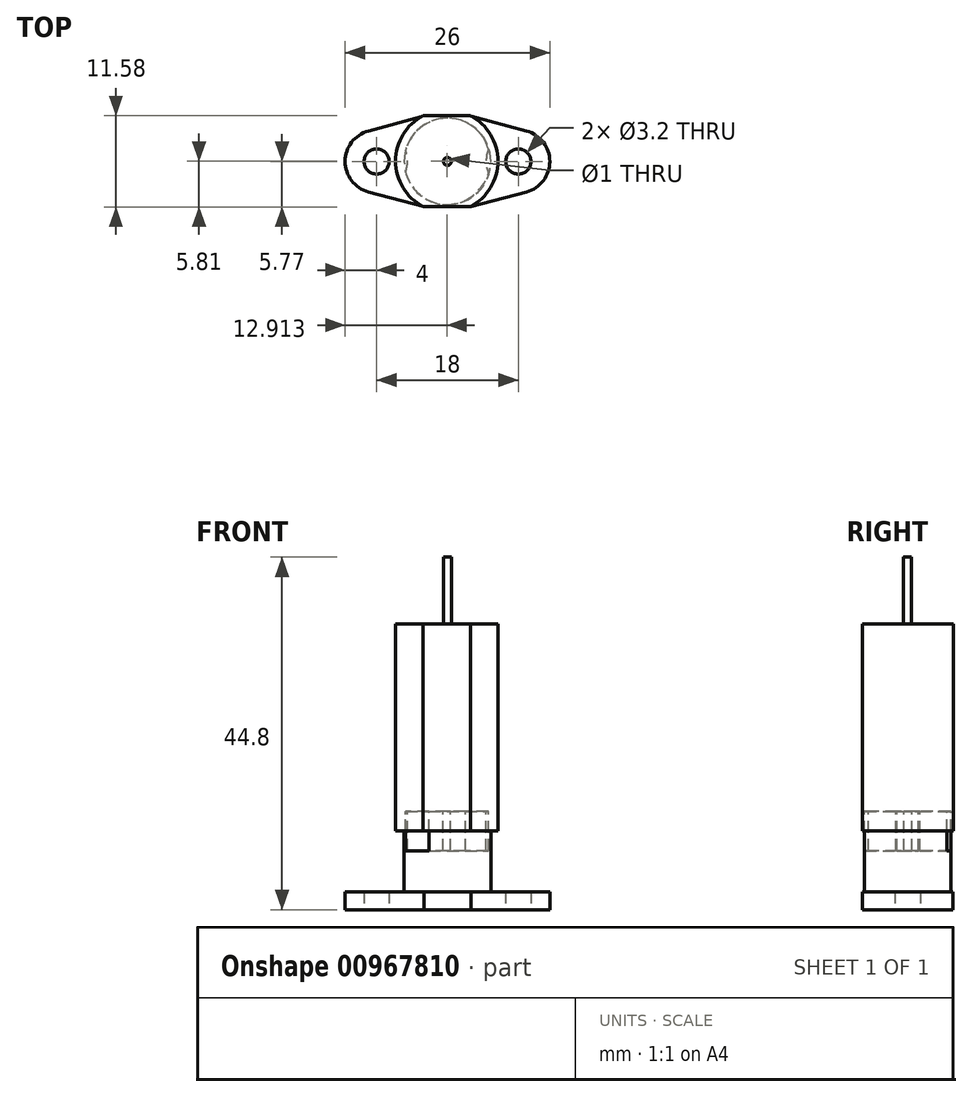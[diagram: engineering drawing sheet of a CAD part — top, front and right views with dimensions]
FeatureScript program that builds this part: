
annotation { "Feature Type Name" : "Feature", "Feature Type Description" : "" }
export const myFeature = defineFeature(function(context is Context, id is Id, definition is map)
    precondition{}
    {
        {
            var Q0;
            Q0=qCreatedBy(makeId("Top.planeOp"),FACE);
            var sketch = newSketch(context, id + "F0", { "sketchPlane" : qUnion([Q0])});
            skCircle(sketch, "E0", {"center": v(9, 0) * mm, "radius": 1.6 * mm});
            skCircle(sketch, "E1", {"center": v(-9, 0) * mm, "radius": 1.6 * mm});
            skCircle(sketch, "E2", {"center": v(9, 0) * mm, "radius": 4 * mm});
            skCircle(sketch, "E3", {"center": v(-9, 0) * mm, "radius": 4 * mm});
            skLineSegment(sketch, "E4.bottom", {"start": v(3, 5.77) * mm, "end": v(-3, 5.77) * mm});
            skLineSegment(sketch, "E4.top", {"start": v(3, -5.76) * mm, "end": v(-3, -5.76) * mm});
            skPoint(sketch, "E4.middle", {"position": v(0, 0) * mm});
            skLineSegment(sketch, "E5", {"start": v(3, 5.77) * mm, "end": v(10.04, 3.86) * mm});
            skLineSegment(sketch, "E6", {"start": v(3, -5.76) * mm, "end": v(10.04, -3.86) * mm});
            skLineSegment(sketch, "E7", {"start": v(-3, -5.76) * mm, "end": v(-10.04, -3.86) * mm});
            skLineSegment(sketch, "E8", {"start": v(-3, 5.77) * mm, "end": v(-10.04, 3.86) * mm});
            skCircle(sketch, "E9", {"center": v(0, 0) * mm, "radius": 6.5 * mm});
            skCircle(sketch, "E10", {"center": v(0, 0) * mm, "radius": 0.5 * mm});
            skCircle(sketch, "E11", {"center": v(0, 0) * mm, "radius": 5.5 * mm});
            skSolve(sketch);
        }
        {
            var Q0;
            Q0=makeQuery(id+"F0.imprint","IMPRINT",FACE,{"disambiguationData":[TD([[makeQuery(id+"F0.imprint","IMPRINT",EDGE,{"derivedFrom":sQuery(id+"F0.wireOp",EDGE,"E1")}),-1.0]])]});
            var Q1;
            {var subQ0=sQuery(id+"F0.wireOp",EDGE,"E8");var subQ1=sQuery(id+"F0.wireOp",EDGE,"E3");var subQ2=makeQuery(id+"F0.imprint","INTERSECT",VERTEX,{"derivedFrom":[subQ1,subQ0]});Q1=makeQuery(id+"F0.imprint","IMPRINT",FACE,{"disambiguationData":[TD([[makeQuery(id+"F0.imprint","IMPRINT",EDGE,{"disambiguationData":[TD([[subQ2,1.0]])],"derivedFrom":subQ1}),-1.0]])]});}
            var Q2;
            {var subQ0=sQuery(id+"F0.wireOp",EDGE,"E9");var subQ1=sQuery(id+"F0.wireOp",EDGE,"E3");var subQ2=makeQuery(id+"F0.imprint","INTERSECT",VERTEX,{"disambiguationData":[OD(0.0)],"derivedFrom":[subQ1,subQ0]});Q2=makeQuery(id+"F0.imprint","IMPRINT",FACE,{"disambiguationData":[TD([[makeQuery(id+"F0.imprint","IMPRINT",EDGE,{"disambiguationData":[TD([[subQ2,1.0]])],"derivedFrom":subQ1}),1.0]])]});}
            var Q3;
            {var subQ0=sQuery(id+"F0.wireOp",EDGE,"E11");var subQ1=sQuery(id+"F0.wireOp",EDGE,"E3");var subQ2=makeQuery(id+"F0.imprint","INTERSECT",VERTEX,{"disambiguationData":[OD(0.0)],"derivedFrom":[subQ1,subQ0]});Q3=makeQuery(id+"F0.imprint","IMPRINT",FACE,{"disambiguationData":[TD([[makeQuery(id+"F0.imprint","IMPRINT",EDGE,{"disambiguationData":[TD([[subQ2,1.0]])],"derivedFrom":subQ1}),1.0]])]});}
            var Q4;
            {var subQ0=sQuery(id+"F0.wireOp",EDGE,"E7");var subQ1=sQuery(id+"F0.wireOp",EDGE,"E3");var subQ2=makeQuery(id+"F0.imprint","INTERSECT",VERTEX,{"derivedFrom":[subQ1,subQ0]});Q4=makeQuery(id+"F0.imprint","IMPRINT",FACE,{"disambiguationData":[TD([[makeQuery(id+"F0.imprint","IMPRINT",EDGE,{"disambiguationData":[TD([[subQ2,-1.0]])],"derivedFrom":subQ1}),-1.0]])]});}
            var Q5;
            {var subQ1=sQuery(id+"F0.wireOp",EDGE,"E4.top");Q5=makeQuery(id+"F0.imprint","IMPRINT",FACE,{"disambiguationData":[TD([[makeQuery(id+"F0.imprint","IMPRINT",EDGE,{"derivedFrom":subQ1}),-1.0]])]});}
            var Q6;
            Q6=makeQuery(id+"F0.imprint","IMPRINT",FACE,{"disambiguationData":[TD([[makeQuery(id+"F0.imprint","IMPRINT",EDGE,{"derivedFrom":sQuery(id+"F0.wireOp",EDGE,"E10")}),-1.0]])]});
            var Q7;
            {var subQ1=sQuery(id+"F0.wireOp",EDGE,"E4.bottom");Q7=makeQuery(id+"F0.imprint","IMPRINT",FACE,{"disambiguationData":[TD([[makeQuery(id+"F0.imprint","IMPRINT",EDGE,{"derivedFrom":subQ1}),1.0]])]});}
            var Q8;
            {var subQ0=sQuery(id+"F0.wireOp",EDGE,"E5");var subQ1=sQuery(id+"F0.wireOp",EDGE,"E2");var subQ2=makeQuery(id+"F0.imprint","INTERSECT",VERTEX,{"derivedFrom":[subQ1,subQ0]});Q8=makeQuery(id+"F0.imprint","IMPRINT",FACE,{"disambiguationData":[TD([[makeQuery(id+"F0.imprint","IMPRINT",EDGE,{"disambiguationData":[TD([[subQ2,-1.0]])],"derivedFrom":subQ1}),-1.0]])]});}
            var Q9;
            {var subQ0=sQuery(id+"F0.wireOp",EDGE,"E11");var subQ1=sQuery(id+"F0.wireOp",EDGE,"E2");var subQ2=makeQuery(id+"F0.imprint","INTERSECT",VERTEX,{"disambiguationData":[OD(0.0)],"derivedFrom":[subQ1,subQ0]});Q9=makeQuery(id+"F0.imprint","IMPRINT",FACE,{"disambiguationData":[TD([[makeQuery(id+"F0.imprint","IMPRINT",EDGE,{"disambiguationData":[TD([[subQ2,-1.0]])],"derivedFrom":subQ1}),1.0]])]});}
            var Q10;
            {var subQ0=sQuery(id+"F0.wireOp",EDGE,"E9");var subQ1=sQuery(id+"F0.wireOp",EDGE,"E2");var subQ2=makeQuery(id+"F0.imprint","INTERSECT",VERTEX,{"disambiguationData":[OD(0.0)],"derivedFrom":[subQ1,subQ0]});Q10=makeQuery(id+"F0.imprint","IMPRINT",FACE,{"disambiguationData":[TD([[makeQuery(id+"F0.imprint","IMPRINT",EDGE,{"disambiguationData":[TD([[subQ2,-1.0]])],"derivedFrom":subQ1}),1.0]])]});}
            var Q11;
            Q11=makeQuery(id+"F0.imprint","IMPRINT",FACE,{"disambiguationData":[TD([[makeQuery(id+"F0.imprint","IMPRINT",EDGE,{"derivedFrom":sQuery(id+"F0.wireOp",EDGE,"E0")}),-1.0]])]});
            var Q12;
            {var subQ0=sQuery(id+"F0.wireOp",EDGE,"E6");var subQ1=sQuery(id+"F0.wireOp",EDGE,"E2");var subQ2=makeQuery(id+"F0.imprint","INTERSECT",VERTEX,{"derivedFrom":[subQ1,subQ0]});Q12=makeQuery(id+"F0.imprint","IMPRINT",FACE,{"disambiguationData":[TD([[makeQuery(id+"F0.imprint","IMPRINT",EDGE,{"disambiguationData":[TD([[subQ2,1.0]])],"derivedFrom":subQ1}),-1.0]])]});}
            extrude(context, id + "F1", {"entities" : qUnion([Q0, Q1, Q2, Q3, Q4, Q5, Q6, Q7, Q8, Q9, Q10, Q11, Q12]), "depth" : 2.3 * mm, "offsetDistance" : 25 * mm});
        }
        {
            var Q0;
            Q0=makeQuery(id+"F0.imprint","IMPRINT",FACE,{"disambiguationData":[TD([[makeQuery(id+"F0.imprint","IMPRINT",EDGE,{"derivedFrom":sQuery(id+"F0.wireOp",EDGE,"E10")}),-1.0]])]});
            var Q1;
            Q1=makeQuery(id+"F0.imprint","IMPRINT",FACE,{"disambiguationData":[TD([[makeQuery(id+"F0.imprint","IMPRINT",EDGE,{"derivedFrom":sQuery(id+"F0.wireOp",EDGE,"E10")}),1.0]])]});
            var Q2;
            {var subQ0=sQuery(id+"F0.wireOp",EDGE,"E11");var subQ1=sQuery(id+"F0.wireOp",EDGE,"E3");var subQ2=makeQuery(id+"F0.imprint","INTERSECT",VERTEX,{"disambiguationData":[OD(0.0)],"derivedFrom":[subQ1,subQ0]});Q2=makeQuery(id+"F0.imprint","IMPRINT",FACE,{"disambiguationData":[TD([[makeQuery(id+"F0.imprint","IMPRINT",EDGE,{"disambiguationData":[TD([[subQ2,1.0]])],"derivedFrom":subQ1}),1.0]])]});}
            var Q3;
            {var subQ0=sQuery(id+"F0.wireOp",EDGE,"E11");var subQ1=sQuery(id+"F0.wireOp",EDGE,"E2");var subQ2=makeQuery(id+"F0.imprint","INTERSECT",VERTEX,{"disambiguationData":[OD(0.0)],"derivedFrom":[subQ1,subQ0]});Q3=makeQuery(id+"F0.imprint","IMPRINT",FACE,{"disambiguationData":[TD([[makeQuery(id+"F0.imprint","IMPRINT",EDGE,{"disambiguationData":[TD([[subQ2,-1.0]])],"derivedFrom":subQ1}),1.0]])]});}
            extrude(context, id + "F2", {"entities" : qUnion([Q0, Q1, Q2, Q3]), "operationType" : NewBodyOperationType.ADD, "depth" : 10 * mm, "offsetDistance" : 25 * mm});
        }
        {
            var Q0;
            Q0=makeQuery(id+"F2.opExtrude","CAP_FACE",FACE,{"disambiguationData":[OSD([sQuery(id+"F0.wireOp",EDGE,"E11")])],"isStart":false});
            var sketch = newSketch(context, id + "F3", { "sketchPlane" : qUnion([Q0])});
            skCircle(sketch, "E12", {"center": v(8.91, 0.04) * mm, "radius": 1.6 * mm});
            skCircle(sketch, "E13", {"center": v(-9.09, 0.04) * mm, "radius": 1.6 * mm});
            skCircle(sketch, "E14", {"center": v(8.91, 0.04) * mm, "radius": 4 * mm});
            skCircle(sketch, "E15", {"center": v(-9.09, 0.04) * mm, "radius": 4 * mm});
            skLineSegment(sketch, "E16.bottom", {"start": v(2.91, 5.8) * mm, "end": v(-3.09, 5.8) * mm});
            skLineSegment(sketch, "E16.top", {"start": v(2.91, -5.72) * mm, "end": v(-3.09, -5.72) * mm});
            skPoint(sketch, "E16.middle", {"position": v(-0.09, 0.04) * mm});
            skLineSegment(sketch, "E17", {"start": v(2.91, 5.8) * mm, "end": v(9.96, 3.9) * mm});
            skLineSegment(sketch, "E18", {"start": v(2.91, -5.72) * mm, "end": v(9.96, -3.82) * mm});
            skLineSegment(sketch, "E19", {"start": v(-3.09, -5.72) * mm, "end": v(-10.13, -3.82) * mm});
            skLineSegment(sketch, "E20", {"start": v(-3.09, 5.8) * mm, "end": v(-10.13, 3.9) * mm});
            skCircle(sketch, "E21", {"center": v(-0.09, 0.04) * mm, "radius": 6.5 * mm});
            skCircle(sketch, "E22", {"center": v(-0.09, 0.04) * mm, "radius": 0.5 * mm});
            skCircle(sketch, "E23", {"center": v(-0.09, 0.04) * mm, "radius": 5.5 * mm});
            skSolve(sketch);
        }
        {
            var Q0;
            Q0=makeQuery(id+"F3.imprint","IMPRINT",FACE,{"disambiguationData":[TD([[makeQuery(id+"F3.imprint","IMPRINT",EDGE,{"derivedFrom":sQuery(id+"F3.wireOp",EDGE,"E22")}),1.0]])]});
            var Q1;
            Q1=makeQuery(id+"F3.imprint","IMPRINT",FACE,{"disambiguationData":[TD([[makeQuery(id+"F3.imprint","IMPRINT",EDGE,{"derivedFrom":sQuery(id+"F3.wireOp",EDGE,"E22")}),-1.0]])]});
            var Q2;
            {var subQ0=sQuery(id+"F3.wireOp",EDGE,"E15");var subQ1=makeQuery(id+"F2.opExtrude","CAP_EDGE",EDGE,{"disambiguationData":[OSD([sQuery(id+"F0.wireOp",EDGE,"E11")])],"isStart":false});var subQ2=makeQuery(id+"F3.imprint","INTERSECT",VERTEX,{"disambiguationData":[OD(0.0)],"derivedFrom":[subQ1,subQ0]});Q2=makeQuery(id+"F3.imprint","IMPRINT",FACE,{"disambiguationData":[TD([[makeQuery(id+"F3.imprint","IMPRINT",EDGE,{"disambiguationData":[TD([[subQ2,1.0]])],"derivedFrom":subQ0}),1.0]])]});}
            var Q3;
            {var subQ0=sQuery(id+"F3.wireOp",EDGE,"E23");var subQ1=sQuery(id+"F3.wireOp",EDGE,"E14");var subQ2=makeQuery(id+"F3.imprint","INTERSECT",VERTEX,{"disambiguationData":[OD(0.0)],"derivedFrom":[subQ1,subQ0]});Q3=makeQuery(id+"F3.imprint","IMPRINT",FACE,{"disambiguationData":[TD([[makeQuery(id+"F3.imprint","IMPRINT",EDGE,{"disambiguationData":[TD([[subQ2,-1.0]])],"derivedFrom":subQ1}),1.0]])]});}
            var Q4;
            {var subQ0=sQuery(id+"F3.wireOp",EDGE,"E21");var subQ1=sQuery(id+"F3.wireOp",EDGE,"E14");var subQ2=makeQuery(id+"F3.imprint","INTERSECT",VERTEX,{"disambiguationData":[OD(0.0)],"derivedFrom":[subQ1,subQ0]});Q4=makeQuery(id+"F3.imprint","IMPRINT",FACE,{"disambiguationData":[TD([[makeQuery(id+"F3.imprint","IMPRINT",EDGE,{"disambiguationData":[TD([[subQ2,-1.0]])],"derivedFrom":subQ1}),1.0]])]});}
            var Q5;
            {var subQ1=sQuery(id+"F3.wireOp",EDGE,"E16.bottom");Q5=makeQuery(id+"F3.imprint","IMPRINT",FACE,{"disambiguationData":[TD([[makeQuery(id+"F3.imprint","IMPRINT",EDGE,{"derivedFrom":subQ1}),1.0]])]});}
            var Q6;
            {var subQ0=sQuery(id+"F3.wireOp",EDGE,"E23");var subQ1=sQuery(id+"F3.wireOp",EDGE,"E15");var subQ2=makeQuery(id+"F3.imprint","INTERSECT",VERTEX,{"disambiguationData":[OD(0.0)],"derivedFrom":[subQ1,subQ0]});Q6=makeQuery(id+"F3.imprint","IMPRINT",FACE,{"disambiguationData":[TD([[makeQuery(id+"F3.imprint","IMPRINT",EDGE,{"disambiguationData":[TD([[subQ2,-1.0]])],"derivedFrom":subQ1}),1.0]])]});}
            var Q7;
            {var subQ0=sQuery(id+"F3.wireOp",EDGE,"E16.top");Q7=makeQuery(id+"F3.imprint","IMPRINT",FACE,{"disambiguationData":[TD([[makeQuery(id+"F3.imprint","IMPRINT",EDGE,{"derivedFrom":subQ0}),-1.0]])]});}
            var Q8;
            {var subQ0=sQuery(id+"F3.wireOp",EDGE,"E23");var subQ1=sQuery(id+"F3.wireOp",EDGE,"E15");var subQ2=makeQuery(id+"F3.imprint","INTERSECT",VERTEX,{"disambiguationData":[OD(0.0)],"derivedFrom":[subQ1,subQ0]});Q8=makeQuery(id+"F3.imprint","IMPRINT",FACE,{"disambiguationData":[TD([[makeQuery(id+"F3.imprint","IMPRINT",EDGE,{"disambiguationData":[TD([[subQ2,1.0]])],"derivedFrom":subQ1}),-1.0]])]});}
            var Q9;
            {var subQ0=sQuery(id+"F3.wireOp",EDGE,"E23");var subQ1=sQuery(id+"F3.wireOp",EDGE,"E15");var subQ2=makeQuery(id+"F3.imprint","INTERSECT",VERTEX,{"disambiguationData":[OD(0.0)],"derivedFrom":[subQ1,subQ0]});Q9=makeQuery(id+"F3.imprint","IMPRINT",FACE,{"disambiguationData":[TD([[makeQuery(id+"F3.imprint","IMPRINT",EDGE,{"disambiguationData":[TD([[subQ2,1.0]])],"derivedFrom":subQ1}),1.0]])]});}
            var Q10;
            {var subQ0=sQuery(id+"F3.wireOp",EDGE,"E23");var subQ1=sQuery(id+"F3.wireOp",EDGE,"E14");var subQ2=makeQuery(id+"F3.imprint","INTERSECT",VERTEX,{"disambiguationData":[OD(0.0)],"derivedFrom":[subQ1,subQ0]});Q10=makeQuery(id+"F3.imprint","IMPRINT",FACE,{"disambiguationData":[TD([[makeQuery(id+"F3.imprint","IMPRINT",EDGE,{"disambiguationData":[TD([[subQ2,1.0]])],"derivedFrom":subQ1}),-1.0]])]});}
            var Q11;
            {var subQ0=sQuery(id+"F3.wireOp",EDGE,"E23");var subQ1=sQuery(id+"F3.wireOp",EDGE,"E14");var subQ2=makeQuery(id+"F3.imprint","INTERSECT",VERTEX,{"disambiguationData":[OD(0.0)],"derivedFrom":[subQ1,subQ0]});Q11=makeQuery(id+"F3.imprint","IMPRINT",FACE,{"disambiguationData":[TD([[makeQuery(id+"F3.imprint","IMPRINT",EDGE,{"disambiguationData":[TD([[subQ2,1.0]])],"derivedFrom":subQ1}),1.0]])]});}
            var Q12;
            {var subQ0=sQuery(id+"F3.wireOp",EDGE,"E23");var subQ1=sQuery(id+"F3.wireOp",EDGE,"E14");var subQ2=makeQuery(id+"F3.imprint","INTERSECT",VERTEX,{"disambiguationData":[OD(1.0)],"derivedFrom":[subQ1,subQ0]});Q12=makeQuery(id+"F3.imprint","IMPRINT",FACE,{"disambiguationData":[TD([[makeQuery(id+"F3.imprint","IMPRINT",EDGE,{"disambiguationData":[TD([[subQ2,-1.0]])],"derivedFrom":subQ1}),-1.0]])]});}
            var Q13;
            {var subQ0=sQuery(id+"F3.wireOp",EDGE,"E23");var subQ1=sQuery(id+"F3.wireOp",EDGE,"E15");var subQ2=makeQuery(id+"F3.imprint","INTERSECT",VERTEX,{"disambiguationData":[OD(1.0)],"derivedFrom":[subQ1,subQ0]});Q13=makeQuery(id+"F3.imprint","IMPRINT",FACE,{"disambiguationData":[TD([[makeQuery(id+"F3.imprint","IMPRINT",EDGE,{"disambiguationData":[TD([[subQ2,-1.0]])],"derivedFrom":subQ1}),-1.0]])]});}
            extrude(context, id + "F4", {"entities" : qUnion([Q0, Q1, Q2, Q3, Q4, Q5, Q6, Q7, Q8, Q9, Q10, Q11, Q12, Q13]), "depth" : 26.3 * mm, "offsetDistance" : 25 * mm});
        }
        {
            var Q0;
            Q0=makeQuery(id+"F0.imprint","IMPRINT",FACE,{"disambiguationData":[TD([[makeQuery(id+"F0.imprint","IMPRINT",EDGE,{"derivedFrom":sQuery(id+"F0.wireOp",EDGE,"E10")}),1.0]])]});
            extrude(context, id + "F5", {"entities" : qUnion([Q0]), "operationType" : NewBodyOperationType.ADD, "depth" : 44.8 * mm, "offsetDistance" : 25 * mm});
        }
        {
            var Q0;
            Q0=makeQuery(id+"F3.imprint","IMPRINT",FACE,{"disambiguationData":[TD([[makeQuery(id+"F3.imprint","IMPRINT",EDGE,{"derivedFrom":sQuery(id+"F3.wireOp",EDGE,"E22")}),-1.0]])]});
            var sketch = newSketch(context, id + "F6", { "sketchPlane" : qUnion([Q0])});
            skSolve(sketch);
        }
        {
            var Q0;
            Q0=makeQuery(id+"F6.imprint","IMPRINT",FACE,{"disambiguationData":[TD([[makeQuery(id+"F6.imprint","IMPRINT",EDGE,{"derivedFrom":makeQuery(id+"F3.imprint","IMPRINT",EDGE,{"derivedFrom":sQuery(id+"F3.wireOp",EDGE,"E22")})}),-1.0]])]});
            extrude(context, id + "F7", {"entities" : qUnion([Q0]), "endBound" : BoundingType.SYMMETRIC, "oppositeDirection" : true, "depth" : 5 * mm, "offsetDistance" : 25 * mm});
        }
    });
